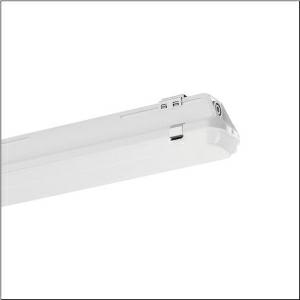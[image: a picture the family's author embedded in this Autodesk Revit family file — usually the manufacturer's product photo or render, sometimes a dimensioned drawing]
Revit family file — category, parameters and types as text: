
# Revit family: monsun_r__12_51fp207p460h_c51f
name_source: partatom
category: Lighting Fixtures
units: mm (PartAtom-declared; Revit-internal decimal feet)

## family parameters
Cut with Voids When Loaded = No
Host = Face
Light Source = No
Part Type = Normal
Room Calculation Point = No
Round Connector Dimension = Use Diameter
Shared = No

## types (1)
- Monsun® 12 (1 x LED, 6030 lm, 37.7 W, 4000K)
    Apparent Load = 38 VA
    CIE Flux Codes = 45 75 93 94 100
    Color Rendering = 80
    Color Temperature = 4000K
    Default Elevation = 1800 mm
    Description = Monsun® 12, damp-proof luminaire, chain hanger, primary optical cover: enclosure, of PC, light emission: direct distribution, primary light characteristic: symmetric, installation type: suspended mounting, surface-mounted, horizontal mounting, vertical mounting, LED rated luminous flux: 6.030 lm, light colour: 840, colour temperature: 4000K, control gear: ECG, with terminal, 3-pole, max. 2.5mm², mains connection: 220..240V, AC, 50/60Hz, rated input power: 38W, luminaire housing, of glass-fibre reinforced polyester, uncoated, bright grey, length: 1.590 mm, width: 90 mm, height: 88mm, clip for enclosure, of stainless steel (V2A), ceiling mounting element, of stainless steel (V2A), chain hanger, of stainless steel (V2A), protection rating (complete): IP66, insulation class (complete): insulation class I (protective earthing), certification: CE, ENEC, VDE, protection symbol: D, impact resistance: IK08, permissible ambient temperature for indoor applications: -35..+40°C, standard: EN 50419, EN 60598-2-1, no direct snow, no direct sun, no direct rain, for indoor or canopied outdoor use, corresponds to IFS (International Featured Standards) requirements for safety and quality in the food industry, packaging unit: 1 piece
    Height = 89 mm
    Lamp = 1 x LED
    Lamp Light Flux = 6030 lm
    Lamp Power = 37.7 W
    Lamp count = 1
    Length = 1590 mm
    Luminous efficacy = 160 lm/W
    Manufacturer = Siteco
    ModVariant = No
    Model = 51FP207P460H
    Mounting Place = Ceiling
    Mounting Type = Pendant
    Number of Poles = 1
    OnlyDefault = Yes
    Power Factor = 1
    Product Name = Monsun® 12
    Product group = damp-proof luminaire | ceiling pendant
    ProductGroupID = 908
    Protection Class = Protection class I
    Protection Degree = IP 66
    RLX_Detail_Level = 1
    RlxData = <blob elided: 88361 chars, md5=5d9b643c>
    Socket = socket
    Standby Power = 0 W
    System Light Flux = 6030 lm
    System Power = 38 W
    Type Comments = Product without accessories
    Type Image = l_1004748.jpg
    URL = http://relux.com
    VarID = ---
    Voltage = 0 V
    Weight = 0.00 kg
    Width = 90 mm

## geometry (parser evidence)
native form markers: Blend x4, Sweep x13
no freeform markers — native parametric forms only
